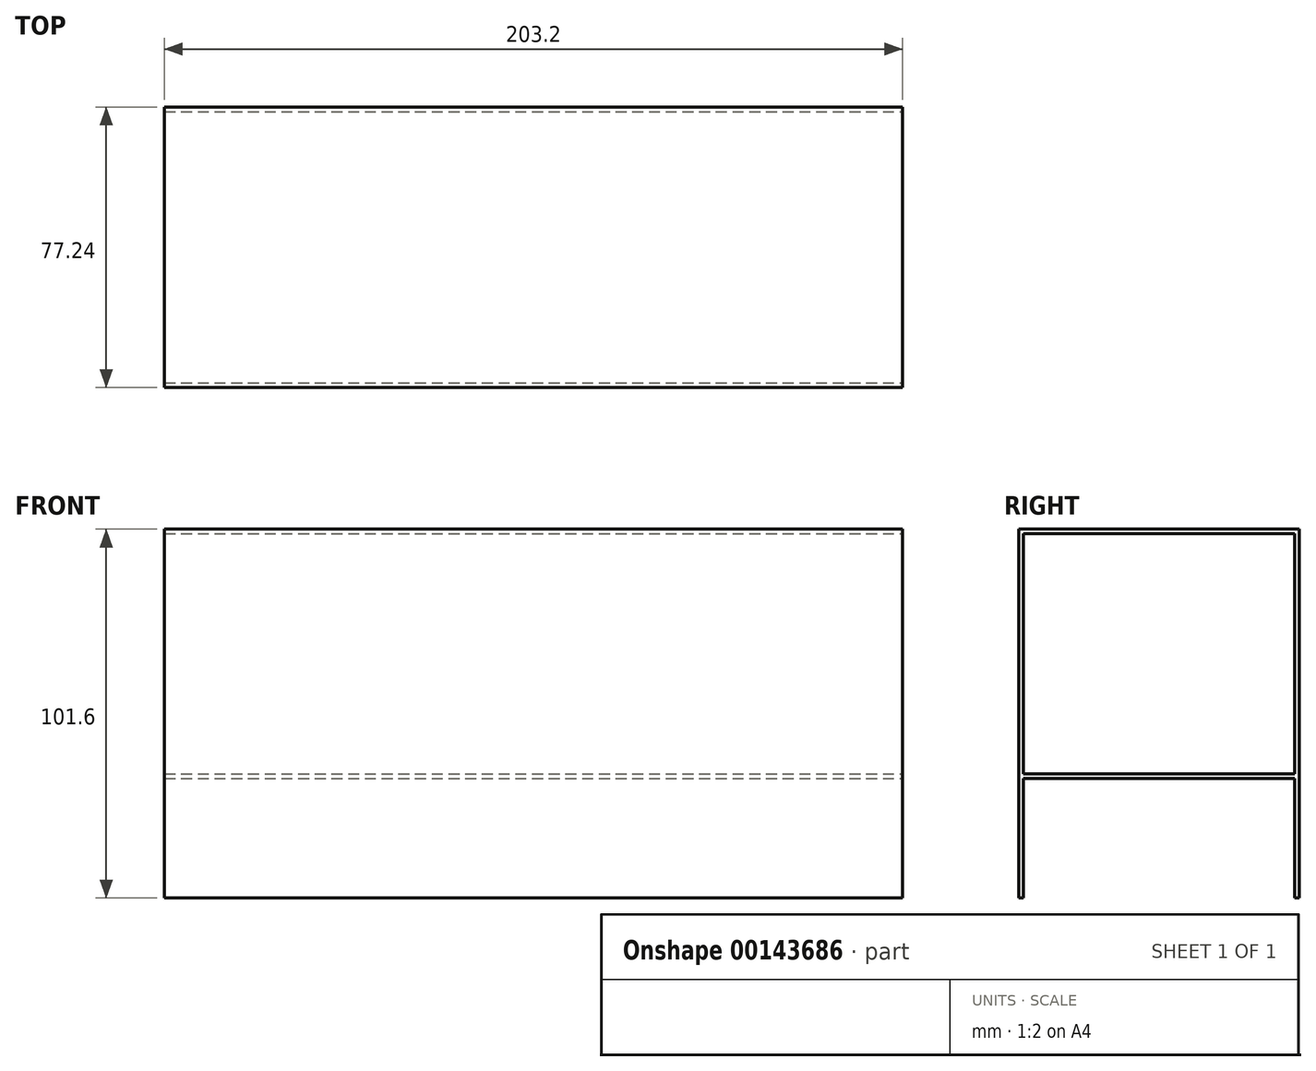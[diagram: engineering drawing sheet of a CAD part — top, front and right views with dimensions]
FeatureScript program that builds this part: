
annotation { "Feature Type Name" : "Feature", "Feature Type Description" : "" }
export const myFeature = defineFeature(function(context is Context, id is Id, definition is map)
    precondition{}
    {
        {
            var Q0;
            Q0=qCreatedBy(makeId("Right.planeOp"),FACE);
            var sketch = newSketch(context, id + "F0", { "sketchPlane" : qUnion([Q0])});
            skLineSegment(sketch, "E0.left", {"start": v(38.62, -50.8) * mm, "end": v(38.62, 50.8) * mm});
            skLineSegment(sketch, "E0.right", {"start": v(-38.62, -50.8) * mm, "end": v(-38.62, 50.8) * mm});
            skPoint(sketch, "E0.middle", {"position": v(0, 0) * mm});
            skLineSegment(sketch, "E1", {"start": v(-37.35, -17.92) * mm, "end": v(37.35, -17.92) * mm});
            skLineSegment(sketch, "E2", {"start": v(-38.62, -50.8) * mm, "end": v(-37.35, -50.8) * mm});
            skLineSegment(sketch, "E3", {"start": v(37.35, -50.8) * mm, "end": v(38.62, -50.8) * mm});
            skLineSegment(sketch, "E4", {"start": v(-38.62, 50.8) * mm, "end": v(38.62, 50.8) * mm});
            skLineSegment(sketch, "E5.0", {"start": v(-37.35, -16.65) * mm, "end": v(37.35, -16.65) * mm});
            skLineSegment(sketch, "E6.0", {"start": v(-37.35, 49.53) * mm, "end": v(37.35, 49.53) * mm});
            skLineSegment(sketch, "E7.0", {"start": v(-37.35, -16.65) * mm, "end": v(-37.35, 49.53) * mm});
            skLineSegment(sketch, "E8.0", {"start": v(37.35, -16.65) * mm, "end": v(37.35, 49.53) * mm});
            skLineSegment(sketch, "E9", {"start": v(-37.35, -17.92) * mm, "end": v(-37.35, -50.8) * mm});
            skLineSegment(sketch, "E10", {"start": v(37.35, -17.92) * mm, "end": v(37.35, -50.8) * mm});
            skSolve(sketch);
        }
        {
            var Q0;
            Q0=sQuery(id+"F0.wireOp",EDGE,"E6.0");
            var Q1;
            Q1=sQuery(id+"F0.wireOp",EDGE,"E7.0");
            var Q2;
            Q2=sQuery(id+"F0.wireOp",EDGE,"E5.0");
            var Q3;
            Q3=sQuery(id+"F0.wireOp",EDGE,"E8.0");
            var Q4;
            Q4=sQuery(id+"F0.wireOp",EDGE,"E0.right");
            var Q5;
            Q5=sQuery(id+"F0.wireOp",EDGE,"E10");
            var Q6;
            Q6=sQuery(id+"F0.wireOp",EDGE,"E9");
            var Q7;
            Q7=sQuery(id+"F0.wireOp",EDGE,"E0.left");
            var Q8;
            Q8=sQuery(id+"F0.wireOp",EDGE,"E1");
            var Q9;
            Q9=sQuery(id+"F0.wireOp",EDGE,"E4");
            var Q10;
            Q10=sQuery(id+"F0.wireOp",EDGE,"E2");
            var Q11;
            Q11=sQuery(id+"F0.wireOp",EDGE,"E3");
            extrude(context, id + "F1", {"bodyType" : ToolBodyType.SURFACE, "surfaceEntities" : qUnion([Q0, Q1, Q2, Q3, Q4, Q5, Q6, Q7, Q8, Q9, Q10, Q11]), "endBound" : BoundingType.SYMMETRIC, "depth" : 203.2 * mm});
        }
    });
